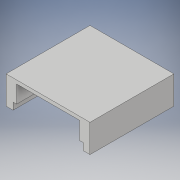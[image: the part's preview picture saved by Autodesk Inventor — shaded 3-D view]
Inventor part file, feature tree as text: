
AUTODESK INVENTOR PART (.ipt)
format: ipt  version: 2019.4 (Build 234330000, 330)  size: 120,832 bytes
history: native  units: in
note: dims shown in document units (in); Inventor stores cm internally (conversion verified against a paired STEP export)
features: extrude x3, sketch x3
ambient origin geometry x8: Origin, YZ Plane, XZ Plane, XY Plane, X Axis, Y Axis, Z Axis, Center Point
bodies: Solid1 (feature_tree)
feature tree (6):
  extrude  "Extrusion1"  Depth=3.0in
  extrude  "Extrusion2"  Depth=1.0in TaperAngle=0.0deg
  extrude  "Extrusion3"  Depth=0.875in TaperAngle=0.0deg
  sketch  "Sketch1"  dims[d0=3.0in d1=1.5in]
  sketch  "Sketch2"  dims[d2=1.5in d3=1.0in d4=0.0in]
  sketch  "Sketch4"  dims[d5=1.125in d6=0.875in d7=0.0in d11=0.25in d14=0.25in d15=6.0in d16=0.0in d17=1.125in d21=0.25in d22=0.25in]
